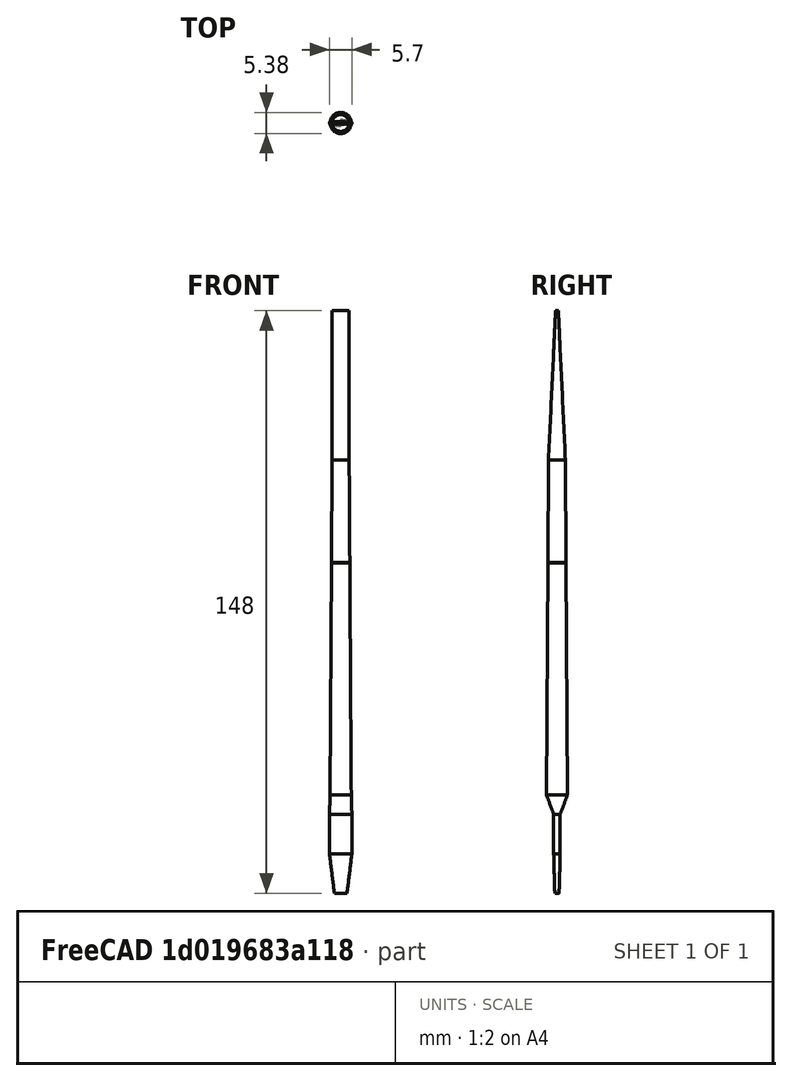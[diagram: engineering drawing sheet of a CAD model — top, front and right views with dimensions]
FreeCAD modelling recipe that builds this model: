
FCSTD DOCUMENT  (FreeCAD 0.21R33675 (Git))
Label: parametric_flattening_shaping_mandrel_1
License: Other
objects: TechDraw::DrawViewDimension×14, TechDraw::DrawGeomHatch×12, Sketcher::SketchObject×8, TechDraw::DrawProjGroupItem×8, TechDraw::DrawViewPart×4, Spreadsheet::Sheet×2, TechDraw::DrawSVGTemplate×2, TechDraw::DrawProjGroup×2, TechDraw::DrawViewBalloon×2, TechDraw::DrawPage×2, PartDesign::AdditiveLoft×1, PartDesign::Groove×1, PartDesign::Body×1, Image::ImagePlane×1
note: 23 computed .brp shape members not serialized (recipe doc carries the construction recipe); baked Part::Feature solids carry a one-line shape summary decoded from their .brp

FEATURE [Sketcher::SketchObject] Sketch  label="s_flattening_staple_eye_locus"
  AttachmentOffset = pos=(0,0,138) rot=(0,0,1;0rad)
  FullyConstrained = true
  MapMode = 5
  Placement = pos=(0,0,138) rot=(0,0,1;0rad)
  Support = -> [XY_Plane]
  expr: .AttachmentOffset.Base.z = Spreadsheet.mandrel_length - Spreadsheet.mandrel_length_prodtruding_above_eye
  expr: Constraints[5] = Spreadsheet.eye_height_internal
  expr: Constraints[6] = Spreadsheet.mandrel_od_at_bottom_of_flattening_taper_on_rod
  sketch-geometry (5):
    g0: Ellipse CenterX=0 CenterY=0 CenterZ=0 NormalX=0 NormalY=0 NormalZ=1 MajorRadius=2.15132 MinorRadius=0.825 AngleXU=0
    g1: LineSegment StartX=2.15132 StartY=0 StartZ=0 EndX=-2.15132 EndY=0 EndZ=0
    g2: LineSegment StartX=0 StartY=0.825 StartZ=0 EndX=0 EndY=-0.825 EndZ=0
    g3: GeomPoint X=1.98684 Y=0 Z=0
    g4: GeomPoint X=-1.98684 Y=0 Z=0
  constraints (5):
    c: InternalAlignment(g1-g4 -> g0) x4
    c: Coincident(g0,g-1)
    c: DistanceY(g2,g2) = 1.65
    c: DistanceX(g1,g1) = 4.30263
    c: Parallel(g1,g-1)
FEATURE [Spreadsheet::Sheet] Spreadsheet  label="spr_dimensions"
  cells = A1='Inputs; D1='Calculated Quantities (editing some of these may cause computation to fail); G1='Reference Dimensions; A2='eye_height_internal; B2(eye_height_internal)==1.65 mm; D2='mandrel_flattening_tip_height; E2(mandrel_flattening_tip_height)==eye_height_internal - mandrel_length_prodtruding_above_eye * (mandrel_od_at_bottom_of_flattening_taper_on_rod - eye_height_internal) / taper_length; A3='eye_width_internal; B3(eye_width_internal)==5.69 mm; D3='mandrel_shaping_taper_length; E3(mandrel_shaping_taper_length)==mandrel_length_prodtruding_above_eye; A4='taper_length; B4(taper_length)==28 mm; D4='mandrel_shaping_taper_tip_height; E4(mandrel_shaping_taper_tip_height)==eye_height_internal * 0.67; A5='mandrel_length; B5(mandrel_length)==148 mm; D5='mandrel_shaping_taper_tip_width; E5(mandrel_shaping_taper_tip_width)==mandrel_od_at_bottom_of_flattening_taper_on_rod * 0.75; A6='staple_length; B6(staple_length)==54 mm; D6='rod_length; E6(rod_length)==mandrel_length - mandrel_length_prodtruding_above_eye - taper_length - mandrel_shaping_taper_length - mandrel_shaping_section_parallel_length - mandrel_shaping_section_to_rod_transition_length; A7='staple_tube_taper_angle; B7(staple_tube_taper_angle)==0.3607 deg; D7='mandrel_od_at_bottom_of_shaping_taper_on_rod; E7(mandrel_od_at_bottom_of_shaping_taper_on_rod)==mandrel_od_at_bottom_of_flattening_taper_on_rod + 2 * rod_length * tan(staple_tube_taper_angle); A8='mandrel_od_at_staple_tube_end; B8(mandrel_od_at_staple_tube_end)==4.63 mm; D8='unflattened_staple_length; E8(unflattened_staple_length)==staple_length - taper_length; D9='mandrel_od_at_bottom_of_flattening_taper_on_rod; E9(mandrel_od_at_bottom_of_flattening_taper_on_rod)==mandrel_od_at_staple_tube_end - 2 * unflattened_staple_length * tan(staple_tube_taper_angle); A12='Custom Inputs - Only adjust if you are clear as to what the effect is; A13='mandrel_length_prodtruding_above_eye; B13(mandrel_length_prodtruding_above_eye)==10 mm; A14='mandrel_shaping_section_parallel_length; B14(mandrel_shaping_section_parallel_length)==10 mm; A15='mandrel_shaping_section_to_rod_transition_length; B15(mandrel_shaping_section_to_rod_transition_length)==5 mm; A16='staple_tube_end_terminus_score_depth; B16(staple_tube_end_terminus_score_depth)==0.1 mm; A17='staple_tube_end_terminus_score_width; B17(staple_tube_end_terminus_score_width)==0.15 mm; A18='staple_tube_end_terminus_score_radial_position_offset; B18(staple_tube_end_terminus_score_radial_position_offset)==staple_tube_end_terminus_score_depth * 0.1
FEATURE [Sketcher::SketchObject] Sketch001  label="s_flattening_taper_terminus"
  AttachmentOffset = pos=(0,0,110) rot=(0,0,1;0rad)
  FullyConstrained = true
  MapMode = 5
  Placement = pos=(0,0,110) rot=(0,0,1;0rad)
  Support = -> [XY_Plane]
  expr: .AttachmentOffset.Base.z = Spreadsheet.mandrel_length - Spreadsheet.mandrel_length_prodtruding_above_eye - Spreadsheet.taper_length
  expr: Constraints[1] = Spreadsheet.mandrel_od_at_bottom_of_flattening_taper_on_rod
  sketch-geometry (1):
    g0: Circle CenterX=0 CenterY=0 CenterZ=0 NormalX=0 NormalY=0 NormalZ=1 AngleXU=0 Radius=2.15132
  constraints (2):
    c: Coincident(g0,g-1)
    c: Diameter(g0) = 4.30263
FEATURE [Sketcher::SketchObject] Sketch002  label="s_shaping_eye_mid_section"
  AttachmentOffset = pos=(0,0,20) rot=(0,0,1;0rad)
  FullyConstrained = true
  MapMode = 5
  Placement = pos=(0,0,20) rot=(0,0,1;0rad)
  Support = -> [XY_Plane]
  expr: .AttachmentOffset.Base.z = Spreadsheet.mandrel_shaping_taper_length + Spreadsheet.mandrel_shaping_section_parallel_length
  expr: Constraints[6] = Spreadsheet.eye_width_internal
  expr: Constraints[7] = Spreadsheet.eye_height_internal
  sketch-geometry (5):
    g0: Ellipse CenterX=0 CenterY=0 CenterZ=0 NormalX=0 NormalY=0 NormalZ=1 MajorRadius=2.845 MinorRadius=0.825 AngleXU=0
    g1: LineSegment StartX=2.845 StartY=0 StartZ=0 EndX=-2.845 EndY=0 EndZ=0
    g2: LineSegment StartX=0 StartY=0.825 StartZ=0 EndX=0 EndY=-0.825 EndZ=0
    g3: GeomPoint X=2.72276 Y=0 Z=0
    g4: GeomPoint X=-2.72276 Y=0 Z=0
  constraints (5):
    c: InternalAlignment(g1-g4 -> g0) x4
    c: Coincident(g0,g-1)
    c: Parallel(g1,g-1)
    c: DistanceX(g1,g1) = 5.69
    c: DistanceY(g2,g2) = 1.65
FEATURE [Sketcher::SketchObject] Sketch003  label="s_shaping_tip"
  FullyConstrained = true
  MapMode = 5
  Support = -> [XY_Plane]
  expr: Constraints[6] = Spreadsheet.mandrel_shaping_taper_tip_width
  expr: Constraints[7] = Spreadsheet.mandrel_shaping_taper_tip_height
  sketch-geometry (5):
    g0: Ellipse CenterX=0 CenterY=0 CenterZ=0 NormalX=0 NormalY=0 NormalZ=1 MajorRadius=1.61349 MinorRadius=0.55275 AngleXU=0
    g1: LineSegment StartX=1.61349 StartY=0 StartZ=0 EndX=-1.61349 EndY=0 EndZ=0
    g2: LineSegment StartX=0 StartY=0.55275 StartZ=0 EndX=0 EndY=-0.55275 EndZ=0
    g3: GeomPoint X=1.51585 Y=0 Z=0
    g4: GeomPoint X=-1.51585 Y=0 Z=0
  constraints (5):
    c: InternalAlignment(g1-g4 -> g0) x4
    c: Coincident(g0,g-1)
    c: Parallel(g1,g-1)
    c: DistanceX(g1,g1) = 3.22698
    c: DistanceY(g2,g2) = 1.1055
FEATURE [Sketcher::SketchObject] Sketch004  label="s_shaping_eye_outer_section"
  AttachmentOffset = pos=(0,0,10) rot=(0,0,1;0rad)
  FullyConstrained = true
  MapMode = 5
  Placement = pos=(0,0,10) rot=(0,0,1;0rad)
  Support = -> [XY_Plane]
  expr: .AttachmentOffset.Base.z = Spreadsheet.mandrel_shaping_taper_length
  expr: Constraints[6] = Spreadsheet.eye_width_internal
  expr: Constraints[7] = Spreadsheet.eye_height_internal
  sketch-geometry (5):
    g0: Ellipse CenterX=0 CenterY=0 CenterZ=0 NormalX=0 NormalY=0 NormalZ=1 MajorRadius=2.845 MinorRadius=0.825 AngleXU=0
    g1: LineSegment StartX=2.845 StartY=0 StartZ=0 EndX=-2.845 EndY=0 EndZ=0
    g2: LineSegment StartX=0 StartY=0.825 StartZ=0 EndX=0 EndY=-0.825 EndZ=0
    g3: GeomPoint X=2.72276 Y=0 Z=0
    g4: GeomPoint X=-2.72276 Y=0 Z=0
  constraints (5):
    c: InternalAlignment(g1-g4 -> g0) x4
    c: Coincident(g0,g-1)
    c: Parallel(g1,g-1)
    c: DistanceX(g1,g1) = 5.69
    c: DistanceY(g2,g2) = 1.65
FEATURE [Sketcher::SketchObject] Sketch005  label="s_shaping_taper_terminus"
  AttachmentOffset = pos=(0,0,25) rot=(0,0,1;0rad)
  FullyConstrained = true
  MapMode = 5
  Placement = pos=(0,0,25) rot=(0,0,1;0rad)
  Support = -> [XY_Plane]
  expr: .AttachmentOffset.Base.z = Spreadsheet.mandrel_shaping_taper_length + Spreadsheet.mandrel_shaping_section_parallel_length + Spreadsheet.mandrel_shaping_section_to_rod_transition_length
  expr: Constraints[1] = Spreadsheet.mandrel_od_at_bottom_of_shaping_taper_on_rod
  sketch-geometry (1):
    g0: Circle CenterX=0 CenterY=0 CenterZ=0 NormalX=0 NormalY=0 NormalZ=1 AngleXU=0 Radius=2.68643
  constraints (2):
    c: Coincident(g0,g-1)
    c: Diameter(g0) = 5.37287
FEATURE [Sketcher::SketchObject] Sketch006  label="s_flattening_tip"
  AttachmentOffset = pos=(0,0,148) rot=(0,0,1;0rad)
  FullyConstrained = true
  MapMode = 5
  Placement = pos=(0,0,148) rot=(0,0,1;0rad)
  Support = -> [XY_Plane]
  expr: .AttachmentOffset.Base.z = Spreadsheet.mandrel_length
  expr: Constraints[5] = Spreadsheet.mandrel_flattening_tip_height
  expr: Constraints[6] = Spreadsheet.mandrel_od_at_bottom_of_flattening_taper_on_rod
  sketch-geometry (5):
    g0: Ellipse CenterX=0 CenterY=0 CenterZ=0 NormalX=0 NormalY=0 NormalZ=1 MajorRadius=2.15132 MinorRadius=0.351315 AngleXU=0
    g1: LineSegment StartX=2.15132 StartY=0 StartZ=0 EndX=-2.15132 EndY=0 EndZ=0
    g2: LineSegment StartX=0 StartY=0.351315 StartZ=0 EndX=0 EndY=-0.351315 EndZ=0
    g3: GeomPoint X=2.12244 Y=0 Z=0
    g4: GeomPoint X=-2.12244 Y=0 Z=0
  constraints (5):
    c: InternalAlignment(g1-g4 -> g0) x4
    c: Coincident(g0,g-1)
    c: DistanceY(g2,g2) = 0.70263
    c: DistanceX(g1,g1) = 4.30263
    c: Parallel(g1,g-1)
FEATURE [PartDesign::AdditiveLoft] AdditiveLoft  label="al_mandrel"
  Closed = false
  Profile = -> Sketch006
  Ruled = true
  Sections = -> [Sketch,Sketch001,Sketch005,Sketch002,Sketch004,Sketch003]
FEATURE [Sketcher::SketchObject] Sketch007  label="s_staple_end_score"
  AttachmentOffset = pos=(2.275,83.925,0) rot=(0,0,1;0rad)
  FullyConstrained = true
  MapMode = 5
  Placement = pos=(2.275,-1.86e-14,83.925) rot=(1,0,0;1.5708rad)
  Support = -> [XZ_Plane]
  expr: .AttachmentOffset.Base.x = Spreadsheet.mandrel_od_at_staple_tube_end / 2 - Spreadsheet.staple_tube_end_terminus_score_depth / 2 + Spreadsheet.staple_tube_end_terminus_score_radial_position_offset
  expr: .AttachmentOffset.Base.y = Spreadsheet.mandrel_length - Spreadsheet.mandrel_length_prodtruding_above_eye - Spreadsheet.staple_length - Spreadsheet.staple_tube_end_terminus_score_width / 2
  expr: Constraints[10] = Spreadsheet.staple_tube_end_terminus_score_depth
  expr: Constraints[9] = Spreadsheet.staple_tube_end_terminus_score_width
  sketch-geometry (4):
    g0: LineSegment StartX=-0.05 StartY=0.075 StartZ=0 EndX=0.05 EndY=0.075 EndZ=0
    g1: LineSegment StartX=0.05 StartY=0.075 StartZ=0 EndX=0.05 EndY=-0.075 EndZ=0
    g2: LineSegment StartX=0.05 StartY=-0.075 StartZ=0 EndX=-0.05 EndY=-0.075 EndZ=0
    g3: LineSegment StartX=-0.05 StartY=-0.075 StartZ=0 EndX=-0.05 EndY=0.075 EndZ=0
  constraints (11):
    c: Coincident(g0,g1)
    c: Coincident(g1,g2)
    c: Coincident(g2,g3)
    c: Coincident(g3,g0)
    c: Horizontal(g0)
    c: Horizontal(g2)
    c: Vertical(g1)
    c: Vertical(g3)
    c: Symmetric(g0,g2,g-1)
    c: DistanceY(g1,g1) = 0.15
    c: DistanceX(g0,g0) = 0.1
FEATURE [PartDesign::Groove] Groove  label="gr_staple_tube_end_score"
  Angle = 360
  Axis = (-3e-16,3e-16,1)
  Base = (0,0,0)
  BaseFeature = -> AdditiveLoft
  Profile = -> Sketch007
  ReferenceAxis = -> Z_Axis
FEATURE [PartDesign::Body] Body  label="b_mandrel"
  Group = -> [Sketch006,Sketch,Sketch001,Sketch005,Sketch002,Sketch004,Sketch003,AdditiveLoft,Sketch007,Groove]
  Origin = -> Origin
  Tip = -> Groove
FEATURE [TechDraw::DrawSVGTemplate] Template002
  EditableTexts = Designed_by_Name=Designed by Name; Drawing_number=Drawing number; FC-Date=Date; FC-SC=1:1; FC-SH=Sheet; FC-Title=Mandrel Named Dimensions; Subtitle=Dimensions spreadsheet input parameters; Weight=Weight
  Height = 210
  Orientation = 1
  Width = 297
FEATURE [TechDraw::DrawProjGroupItem] ProjItem  label="v_widths"
  CoarseView = false
  Direction = (0,-1,0)
  Focus = 100
  HardHidden = false
  IsoCount = 0
  IsoHidden = false
  IsoVisible = false
  LockPosition = true
  Perspective = false
  Rotation = 0
  RotationVector = (1,0,0)
  ScaleType = 2
  ScrubCount = 0
  SeamHidden = false
  SeamVisible = true
  SmoothHidden = false
  SmoothVisible = true
  Source = -> [Body]
  Type = 0
  X = 0
  XDirection = (1,0,0)
  Y = 0
FEATURE [TechDraw::DrawProjGroupItem] ProjItem001  label="v_heights"
  CoarseView = false
  Direction = (-1,-1e-16,0)
  Focus = 100
  HardHidden = false
  IsoCount = 0
  IsoHidden = false
  IsoVisible = false
  LockPosition = false
  Perspective = false
  Rotation = 0
  RotationVector = (1,0,0)
  ScaleType = 2
  ScrubCount = 0
  SeamHidden = false
  SeamVisible = true
  SmoothHidden = false
  SmoothVisible = true
  Source = -> [Body]
  Type = 1
  X = -26.0626
  XDirection = (1e-16,-1,0)
  Y = 0
FEATURE [TechDraw::DrawProjGroupItem] ProjItem002  label="Top"
  CoarseView = false
  Direction = (0,0,1)
  Focus = 100
  HardHidden = false
  IsoCount = 0
  IsoHidden = false
  IsoVisible = false
  LockPosition = false
  Perspective = false
  Rotation = 0
  RotationVector = (1,0,0)
  ScaleType = 2
  ScrubCount = 0
  SeamHidden = false
  SeamVisible = true
  SmoothHidden = false
  SmoothVisible = true
  Source = -> [Body]
  Type = 4
  X = 0
  XDirection = (1,0,0)
  Y = -85.9807
FEATURE [TechDraw::DrawProjGroupItem] ProjItem003  label="Bottom"
  CoarseView = false
  Direction = (0,0,-1)
  Focus = 100
  HardHidden = false
  IsoCount = 0
  IsoHidden = false
  IsoVisible = false
  LockPosition = false
  Perspective = false
  Rotation = 0
  RotationVector = (1,0,0)
  ScaleType = 2
  ScrubCount = 0
  SeamHidden = false
  SeamVisible = true
  SmoothHidden = false
  SmoothVisible = true
  Source = -> [Body]
  Type = 5
  X = 0
  XDirection = (1,0,0)
  Y = 85.5632
FEATURE [TechDraw::DrawProjGroup] ProjGroup
  Anchor = -> ProjItem
  AutoDistribute = false
  LockPosition = false
  ProjectionType = 0
  Rotation = 0
  ScaleType = 0
  Source = -> [Body]
  Views = -> [ProjItem,ProjItem001,ProjItem002,ProjItem003]
  X = 100.332
  Y = 105.315
  spacingX = 15
  spacingY = 15
FEATURE [TechDraw::DrawViewPart] View  label="v_lengths"
  CoarseView = false
  Direction = (0,-1,0)
  Focus = 100
  HardHidden = false
  IsoCount = 0
  IsoHidden = false
  IsoVisible = false
  LockPosition = false
  Perspective = false
  Rotation = 0
  ScaleType = 0
  ScrubCount = 0
  SeamHidden = false
  SeamVisible = true
  SmoothHidden = false
  SmoothVisible = true
  Source = -> [Body]
  X = 202.891
  XDirection = (0,0,1)
  Y = 130.162
FEATURE [TechDraw::DrawGeomHatch] GeomHatch  label="GeomHatchFX3"
  FilePattern = <path>
  NamePattern = Diamond
  PatternOffset = (0,0,0)
  PatternRotation = 0
  ScalePattern = 1
  Source = -> ProjItem001 [Face3]
FEATURE [TechDraw::DrawGeomHatch] GeomHatch001  label="GeomHatch001FX2"
  FilePattern = <path>
  NamePattern = Diamond
  PatternOffset = (0,0,0)
  PatternRotation = 0
  ScalePattern = 1
  Source = -> ProjItem001 [Face2]
FEATURE [TechDraw::DrawGeomHatch] GeomHatch002  label="GeomHatch002FX2"
  FilePattern = <path>
  NamePattern = Diamond
  PatternOffset = (0,0,0)
  PatternRotation = 0
  ScalePattern = 1
  Source = -> ProjItem [Face2]
FEATURE [TechDraw::DrawGeomHatch] GeomHatch003  label="GeomHatch003FX3"
  FilePattern = <path>
  NamePattern = Diamond
  PatternOffset = (0,0,0)
  PatternRotation = 0
  ScalePattern = 1
  Source = -> ProjItem [Face3]
FEATURE [TechDraw::DrawGeomHatch] GeomHatch004  label="GeomHatch004FX3"
  FilePattern = <path>
  NamePattern = Diamond
  PatternOffset = (0,0,0)
  PatternRotation = 0
  ScalePattern = 1
  Source = -> View [Face3]
FEATURE [TechDraw::DrawGeomHatch] GeomHatch005  label="GeomHatch005FX2"
  FilePattern = <path>
  NamePattern = Diamond
  PatternOffset = (0,0,0)
  PatternRotation = 0
  ScalePattern = 1
  Source = -> View [Face2]
FEATURE [TechDraw::DrawViewPart] View001  label="v_stapleTubeTaperAngle"
  Caption = Staple Tube Taper Angle
  CoarseView = false
  Direction = (0,-1,0)
  Focus = 100
  HardHidden = false
  IsoCount = 0
  IsoHidden = false
  IsoVisible = false
  LockPosition = false
  Perspective = false
  Rotation = 0
  ScaleType = 0
  ScrubCount = 0
  SeamHidden = false
  SeamVisible = true
  SmoothHidden = false
  SmoothVisible = true
  Source = -> [Body]
  X = 209.983
  XDirection = (0,0,1)
  Y = 184.495
FEATURE [TechDraw::DrawViewDimension] Dimension018
  AngleOverride = false
  Arbitrary = true
  ArbitraryTolerances = false
  EqualTolerance = true
  ExtensionAngle = 0
  FormatSpec = staple_tube_taper_angle
  FormatSpecOverTolerance = %+.2f
  FormatSpecUnderTolerance = %+.2f
  Inverted = false
  LineAngle = 0
  LockPosition = false
  MeasureType = 1
  OverTolerance = 0
  References2D = -> [View001]
  Rotation = 0
  ScaleType = 0
  TheoreticalExact = false
  Type = 6
  UnderTolerance = 0
  X = -31.9116
  Y = 9.19347
  expr: FormatSpec = Spreadsheet.A7
FEATURE [TechDraw::DrawProjGroupItem] ProjItem004  label="v_widths001"
  CoarseView = false
  Direction = (0,-1,0)
  Focus = 100
  HardHidden = false
  IsoCount = 0
  IsoHidden = false
  IsoVisible = false
  LockPosition = true
  Perspective = false
  Rotation = 0
  RotationVector = (1,0,0)
  ScaleType = 2
  ScrubCount = 0
  SeamHidden = false
  SeamVisible = true
  SmoothHidden = false
  SmoothVisible = true
  Source = -> [Body]
  Type = 0
  X = 0
  XDirection = (1,0,0)
  Y = 0
FEATURE [TechDraw::DrawProjGroupItem] ProjItem005  label="v_heights001"
  CoarseView = false
  Direction = (-1,-1e-16,0)
  Focus = 100
  HardHidden = false
  IsoCount = 0
  IsoHidden = false
  IsoVisible = false
  LockPosition = false
  Perspective = false
  Rotation = 0
  RotationVector = (1,0,0)
  ScaleType = 2
  ScrubCount = 0
  SeamHidden = false
  SeamVisible = true
  SmoothHidden = false
  SmoothVisible = true
  Source = -> [Body]
  Type = 1
  X = -26.0626
  XDirection = (1e-16,-1,0)
  Y = 0
FEATURE [TechDraw::DrawProjGroupItem] ProjItem006  label="Top001"
  CoarseView = false
  Direction = (0,0,1)
  Focus = 100
  HardHidden = false
  IsoCount = 0
  IsoHidden = false
  IsoVisible = false
  LockPosition = false
  Perspective = false
  Rotation = 0
  RotationVector = (1,0,0)
  ScaleType = 2
  ScrubCount = 0
  SeamHidden = false
  SeamVisible = true
  SmoothHidden = false
  SmoothVisible = true
  Source = -> [Body]
  Type = 4
  X = 0
  XDirection = (1,0,0)
  Y = -85.0933
FEATURE [TechDraw::DrawProjGroupItem] ProjItem007  label="Bottom001"
  CoarseView = false
  Direction = (0,0,-1)
  Focus = 100
  HardHidden = false
  IsoCount = 0
  IsoHidden = false
  IsoVisible = false
  LockPosition = false
  Perspective = false
  Rotation = 0
  RotationVector = (1,0,0)
  ScaleType = 2
  ScrubCount = 0
  SeamHidden = false
  SeamVisible = true
  SmoothHidden = false
  SmoothVisible = true
  Source = -> [Body]
  Type = 5
  X = 0
  XDirection = (1,0,0)
  Y = 84.9908
FEATURE [TechDraw::DrawProjGroup] ProjGroup001
  Anchor = -> ProjItem004
  AutoDistribute = false
  LockPosition = false
  ProjectionType = 0
  Rotation = 0
  ScaleType = 0
  Source = -> [Body]
  Views = -> [ProjItem004,ProjItem005,ProjItem006,ProjItem007]
  X = 100.332
  Y = 105.315
  spacingX = 15
  spacingY = 15
FEATURE [TechDraw::DrawSVGTemplate] Template003
  EditableTexts = Designed_by_Name=Designed by Name; Drawing_number=Drawing number; FC-Date=Date; FC-SC=1:1; FC-SH=Sheet; FC-Title=Mandrel Dimensions; Subtitle=All dimensions in mm unless otherwise stated; Weight=Weight
  Height = 210
  Orientation = 1
  Width = 297
FEATURE [TechDraw::DrawViewPart] View002  label="v_lengths001"
  CoarseView = false
  Direction = (0,-1,0)
  Focus = 100
  HardHidden = false
  IsoCount = 0
  IsoHidden = false
  IsoVisible = false
  LockPosition = false
  Perspective = false
  Rotation = 0
  ScaleType = 0
  ScrubCount = 0
  SeamHidden = false
  SeamVisible = true
  SmoothHidden = false
  SmoothVisible = true
  Source = -> [Body]
  X = 206.808
  XDirection = (0,0,1)
  Y = 127.902
FEATURE [TechDraw::DrawViewDimension] Dimension030
  AngleOverride = false
  Arbitrary = false
  ArbitraryTolerances = false
  EqualTolerance = true
  ExtensionAngle = 0
  FormatSpec = %.2f
  FormatSpecOverTolerance = %+.2f
  FormatSpecUnderTolerance = %+.2f
  Inverted = false
  LineAngle = 0
  LockPosition = false
  MeasureType = 1
  OverTolerance = 0
  References2D = -> [View002]
  Rotation = 0
  ScaleType = 0
  TheoreticalExact = false
  Type = 1
  UnderTolerance = 0
  X = 2.08367
  Y = -36.7809
FEATURE [TechDraw::DrawViewDimension] Dimension031
  AngleOverride = false
  Arbitrary = false
  ArbitraryTolerances = false
  EqualTolerance = true
  ExtensionAngle = 0
  FormatSpec = %.2f
  FormatSpecOverTolerance = %+.2f
  FormatSpecUnderTolerance = %+.2f
  Inverted = false
  LineAngle = 0
  LockPosition = false
  MeasureType = 1
  OverTolerance = 0
  References2D = -> [View002]
  Rotation = 0
  ScaleType = 0
  TheoreticalExact = false
  Type = 1
  UnderTolerance = 0
  X = -57.3585
  Y = -11.3966
FEATURE [TechDraw::DrawViewDimension] Dimension032
  AngleOverride = false
  Arbitrary = false
  ArbitraryTolerances = false
  EqualTolerance = true
  ExtensionAngle = 0
  FormatSpec = %.2f
  FormatSpecOverTolerance = %+.2f
  FormatSpecUnderTolerance = %+.2f
  Inverted = false
  LineAngle = 0
  LockPosition = false
  MeasureType = 1
  OverTolerance = 0
  References2D = -> [View002]
  Rotation = 0
  ScaleType = 0
  TheoreticalExact = false
  Type = 1
  UnderTolerance = 0
  X = -48.1354
  Y = -20.5559
FEATURE [TechDraw::DrawViewDimension] Dimension033
  AngleOverride = false
  Arbitrary = false
  ArbitraryTolerances = false
  EqualTolerance = true
  ExtensionAngle = 0
  FormatSpec = %.2f
  FormatSpecOverTolerance = %+.2f
  FormatSpecUnderTolerance = %+.2f
  Inverted = false
  LineAngle = 0
  LockPosition = false
  MeasureType = 1
  OverTolerance = 0
  References2D = -> [View002]
  Rotation = 0
  ScaleType = 0
  TheoreticalExact = false
  Type = 1
  UnderTolerance = 0
  X = 25.6815
  Y = -28.036
FEATURE [TechDraw::DrawViewDimension] Dimension034
  AngleOverride = false
  Arbitrary = false
  ArbitraryTolerances = false
  EqualTolerance = true
  ExtensionAngle = 0
  FormatSpec = %.2f
  FormatSpecOverTolerance = %+.2f
  FormatSpecUnderTolerance = %+.2f
  Inverted = false
  LineAngle = 0
  LockPosition = false
  MeasureType = 1
  OverTolerance = 0
  References2D = -> [View002]
  Rotation = 0
  ScaleType = 0
  TheoreticalExact = false
  Type = 1
  UnderTolerance = 0
  X = 57.1294
  Y = -12.0677
FEATURE [TechDraw::DrawViewDimension] Dimension035
  AngleOverride = false
  Arbitrary = false
  ArbitraryTolerances = false
  EqualTolerance = true
  ExtensionAngle = 0
  FormatSpec = %.2f
  FormatSpecOverTolerance = %+.2f
  FormatSpecUnderTolerance = %+.2f
  Inverted = false
  LineAngle = 0
  LockPosition = false
  MeasureType = 1
  OverTolerance = 0
  References2D = -> [View002]
  Rotation = 0
  ScaleType = 0
  TheoreticalExact = false
  Type = 1
  UnderTolerance = 0
  X = 39.7607
  Y = -20.6362
FEATURE [TechDraw::DrawViewPart] View003  label="v_stapleTubeTaperAngle001"
  Caption = Staple Tube Taper Angle
  CoarseView = false
  Direction = (0,-1,0)
  Focus = 100
  HardHidden = false
  IsoCount = 0
  IsoHidden = false
  IsoVisible = false
  LockPosition = false
  Perspective = false
  Rotation = 0
  ScaleType = 0
  ScrubCount = 0
  SeamHidden = false
  SeamVisible = true
  SmoothHidden = false
  SmoothVisible = true
  Source = -> [Body]
  X = 204.958
  XDirection = (0,0,1)
  Y = 184.495
FEATURE [TechDraw::DrawGeomHatch] GeomHatch006  label="GeomHatch006FX3"
  FilePattern = <path>
  NamePattern = Diamond
  PatternOffset = (0,0,0)
  PatternRotation = 0
  ScalePattern = 1
  Source = -> View001 [Face3]
FEATURE [TechDraw::DrawGeomHatch] GeomHatch007  label="GeomHatch007FX2"
  FilePattern = <path>
  NamePattern = Diamond
  PatternOffset = (0,0,0)
  PatternRotation = 0
  ScalePattern = 1
  Source = -> View001 [Face2]
FEATURE [TechDraw::DrawGeomHatch] GeomHatch008  label="GeomHatch008FX2"
  FilePattern = <path>
  NamePattern = Diamond
  PatternOffset = (0,0,0)
  PatternRotation = 0
  ScalePattern = 1
  Source = -> View003 [Face2,Face3]
FEATURE [TechDraw::DrawGeomHatch] GeomHatch009  label="GeomHatch009FX3"
  FilePattern = <path>
  NamePattern = Diamond
  PatternOffset = (0,0,0)
  PatternRotation = 0
  ScalePattern = 1
  Source = -> View002 [Face3,Face2]
FEATURE [TechDraw::DrawGeomHatch] GeomHatch010  label="GeomHatch010FX2"
  FilePattern = <path>
  NamePattern = Diamond
  PatternOffset = (0,0,0)
  PatternRotation = 0
  ScalePattern = 1
  Source = -> ProjItem004 [Face2,Face3]
FEATURE [TechDraw::DrawGeomHatch] GeomHatch011  label="GeomHatch011FX2"
  FilePattern = <path>
  NamePattern = Diamond
  PatternOffset = (0,0,0)
  PatternRotation = 0
  ScalePattern = 1
  Source = -> ProjItem005 [Face2,Face3]
FEATURE [TechDraw::DrawViewBalloon] Balloon
  BubbleShape = 0
  EndType = 0
  EndTypeScale = 1
  KinkLength = 5
  LockPosition = false
  OriginX = 0.421219
  OriginY = 38.5123
  Rotation = 0
  ScaleType = 0
  ShapeScale = 1
  SourceView = -> ProjItem
  Text = staple
  TextWrapLen = -1
  X = 24.2086
  Y = 67.6722
FEATURE [TechDraw::DrawViewBalloon] Balloon001
  BubbleShape = 0
  EndType = 0
  EndTypeScale = 1
  KinkLength = 5
  LockPosition = false
  OriginX = -0.276139
  OriginY = 36.773
  Rotation = 0
  ScaleType = 0
  ShapeScale = 1
  SourceView = -> ProjItem004
  Text = staple
  TextWrapLen = -1
  X = 41.3829
  Y = 48.2641
FEATURE [TechDraw::DrawPage] Page003  label="td_mandrel_dimensionValues"
  KeepUpdated = true
  NextBalloonIndex = 2
  ProjectionType = 0
  Template = -> Template003
  Views = -> [ProjGroup001,View002,Dimension030,Dimension031,Dimension032,Dimension033,Dimension034,Dimension035,View003,Balloon001]
FEATURE [TechDraw::DrawViewDimension] Dimension
  AngleOverride = false
  Arbitrary = true
  ArbitraryTolerances = false
  EqualTolerance = true
  ExtensionAngle = 0
  FormatSpec = mandrel_length
  FormatSpecOverTolerance = %+.2f
  FormatSpecUnderTolerance = %+.2f
  Inverted = false
  LineAngle = 0
  LockPosition = false
  MeasureType = 1
  OverTolerance = 0
  References2D = -> [View]
  Rotation = 0
  ScaleType = 0
  TheoreticalExact = false
  Type = 1
  UnderTolerance = 0
  X = 0.313216
  Y = -42.3232
  expr: FormatSpec = Spreadsheet.A5
FEATURE [TechDraw::DrawViewDimension] Dimension036
  AngleOverride = false
  Arbitrary = true
  ArbitraryTolerances = false
  EqualTolerance = true
  ExtensionAngle = 0
  FormatSpec = staple_length
  FormatSpecOverTolerance = %+.2f
  FormatSpecUnderTolerance = %+.2f
  Inverted = false
  LineAngle = 0
  LockPosition = false
  MeasureType = 1
  OverTolerance = 0
  References2D = -> [View]
  Rotation = 0
  ScaleType = 0
  TheoreticalExact = false
  Type = 1
  UnderTolerance = 0
  X = 36.2068
  Y = -24.381
  expr: FormatSpec = Spreadsheet.A6
FEATURE [TechDraw::DrawViewDimension] Dimension037
  AngleOverride = false
  Arbitrary = true
  ArbitraryTolerances = false
  EqualTolerance = true
  ExtensionAngle = 0
  FormatSpec = taper_length
  FormatSpecOverTolerance = %+.2f
  FormatSpecUnderTolerance = %+.2f
  Inverted = false
  LineAngle = 0
  LockPosition = false
  MeasureType = 1
  OverTolerance = 0
  References2D = -> [View]
  Rotation = 0
  ScaleType = 0
  TheoreticalExact = false
  Type = 1
  UnderTolerance = 0
  X = 47.9843
  Y = 16.3459
  expr: FormatSpec = Spreadsheet.A4
FEATURE [TechDraw::DrawViewDimension] Dimension038
  AngleOverride = false
  Arbitrary = true
  ArbitraryTolerances = false
  EqualTolerance = true
  ExtensionAngle = 0
  FormatSpec = eye_width_internal
  FormatSpecOverTolerance = %+.2f
  FormatSpecUnderTolerance = %+.2f
  Inverted = false
  LineAngle = 0
  LockPosition = false
  MeasureType = 1
  OverTolerance = 0
  References2D = -> [ProjItem]
  Rotation = 0
  ScaleType = 0
  TheoreticalExact = false
  Type = 1
  UnderTolerance = 0
  X = 22.853
  Y = -60.6688
  expr: FormatSpec = Spreadsheet.A3
FEATURE [TechDraw::DrawViewDimension] Dimension039
  AngleOverride = false
  Arbitrary = true
  ArbitraryTolerances = false
  EqualTolerance = true
  ExtensionAngle = 0
  FormatSpec = mandrel_od_at_staple_tube_end
  FormatSpecOverTolerance = %+.2f
  FormatSpecUnderTolerance = %+.2f
  Inverted = false
  LineAngle = 0
  LockPosition = false
  MeasureType = 1
  OverTolerance = 0
  References2D = -> [ProjItem]
  Rotation = 0
  ScaleType = 0
  TheoreticalExact = false
  Type = 1
  UnderTolerance = 0
  X = 27.3275
  Y = 12.4417
  expr: FormatSpec = Spreadsheet.A8
FEATURE [TechDraw::DrawViewDimension] Dimension040
  AngleOverride = false
  Arbitrary = true
  ArbitraryTolerances = false
  EqualTolerance = true
  ExtensionAngle = 0
  FormatSpec = eye_height_internal
  FormatSpecOverTolerance = %+.2f
  FormatSpecUnderTolerance = %+.2f
  Inverted = false
  LineAngle = 0
  LockPosition = false
  MeasureType = 1
  OverTolerance = 0
  References2D = -> [ProjItem001]
  Rotation = 0
  ScaleType = 0
  TheoreticalExact = false
  Type = 1
  UnderTolerance = 0
  X = -34.5073
  Y = 68.6081
  expr: FormatSpec = Spreadsheet.A2
FEATURE [TechDraw::DrawViewDimension] Dimension041
  AngleOverride = false
  Arbitrary = true
  ArbitraryTolerances = false
  EqualTolerance = true
  ExtensionAngle = 0
  FormatSpec = eye_height_internal
  FormatSpecOverTolerance = %+.2f
  FormatSpecUnderTolerance = %+.2f
  Inverted = false
  LineAngle = 0
  LockPosition = false
  MeasureType = 1
  OverTolerance = 0
  References2D = -> [ProjItem001]
  Rotation = 0
  ScaleType = 0
  TheoreticalExact = false
  Type = 1
  UnderTolerance = 0
  X = -37.4428
  Y = -59.2136
  expr: FormatSpec = Spreadsheet.A2
FEATURE [TechDraw::DrawPage] Page002  label="td_mandrel_dimensionNames"
  KeepUpdated = true
  NextBalloonIndex = 2
  ProjectionType = 0
  Template = -> Template002
  Views = -> [ProjGroup,View,View001,Dimension018,Balloon,Dimension,Dimension036,Dimension037,Dimension038,Dimension039,Dimension040,Dimension041]
FEATURE [Image::ImagePlane] dimensionNames  label="README_spr_dimensions"
  XSize = 464.021
  YSize = 328.042
FEATURE [Spreadsheet::Sheet] Spreadsheet001  label="LICENSE"
  cells = A1='Licensed under the TAPR Open Hardware License (www.tapr.org/OHL)
note: 12 file-system paths scrubbed to <path> (originals preserved in the JSON sidecar)
